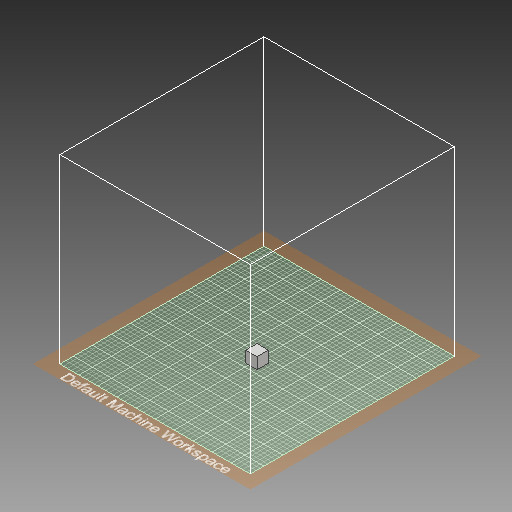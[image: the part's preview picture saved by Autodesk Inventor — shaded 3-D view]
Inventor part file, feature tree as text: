
AUTODESK INVENTOR PART (.ipt)
format: ipt  version: 2019 (Build 230136000, 136)  size: 216,576 bytes
history: native  units: mm
features: extrude x1, sketch x1
ambient origin geometry x8: Origin, YZ Plane, XZ Plane, XY Plane, X Axis, Y Axis, Z Axis, Center Point
bodies: Solid1 (feature_tree)
feature tree (2):
  extrude  "Extrusion1"  Depth=20.0mm
  sketch  "Sketch1"  dims[d0=20.0mm d1=20.0mm d2=20.0mm d3=0.0mm]
